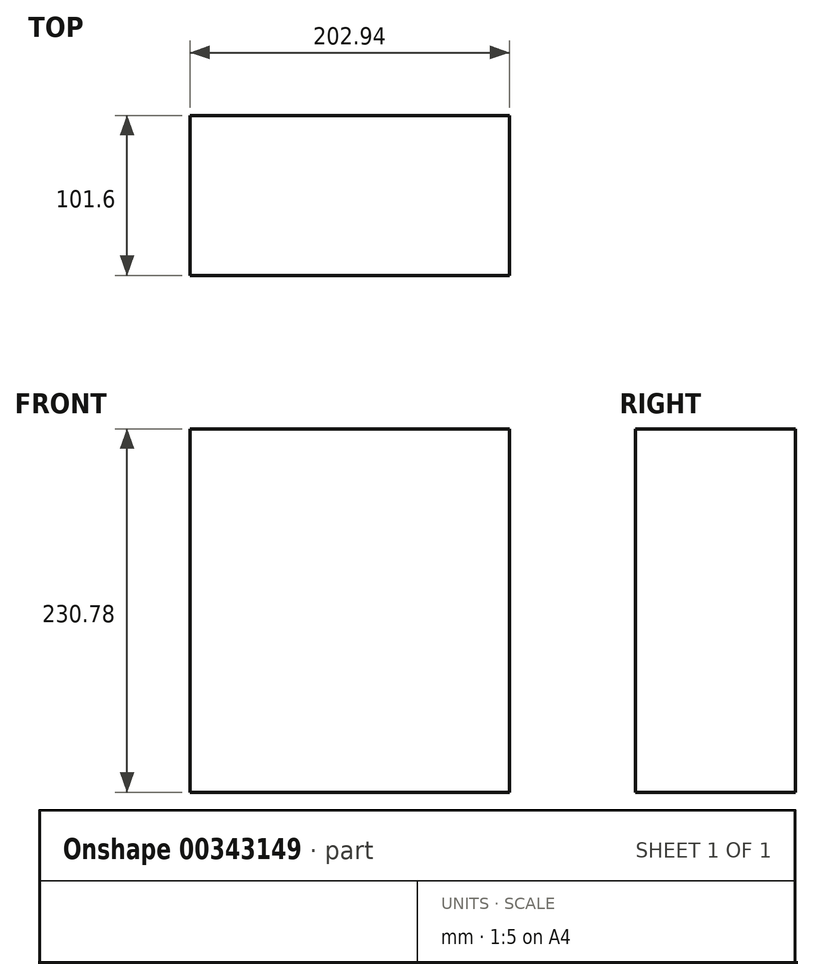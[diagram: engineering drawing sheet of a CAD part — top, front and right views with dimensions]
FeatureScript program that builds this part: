
annotation { "Feature Type Name" : "Feature", "Feature Type Description" : "" }
export const myFeature = defineFeature(function(context is Context, id is Id, definition is map)
    precondition{}
    {
        {
            var Q0;
            Q0=qCreatedBy(makeId("Front.planeOp"),FACE);
            var sketch = newSketch(context, id + "F0", { "sketchPlane" : qUnion([Q0])});
            skLineSegment(sketch, "E0.bottom", {"start": v(101.47, 115.4) * mm, "end": v(-101.47, 115.4) * mm});
            skLineSegment(sketch, "E0.top", {"start": v(101.47, -115.4) * mm, "end": v(-101.47, -115.4) * mm});
            skLineSegment(sketch, "E0.left", {"start": v(-101.47, -115.4) * mm, "end": v(-101.47, 115.4) * mm});
            skLineSegment(sketch, "E0.right", {"start": v(101.47, -115.4) * mm, "end": v(101.47, 115.4) * mm});
            skPoint(sketch, "E0.middle", {"position": v(0, 0) * mm});
            skSolve(sketch);
        }
        {
            var Q0;
            Q0=makeQuery(id+"F0.imprint","IMPRINT",FACE,{"disambiguationData":[TD([[makeQuery(id+"F0.imprint","IMPRINT",EDGE,{"derivedFrom":sQuery(id+"F0.wireOp",EDGE,"E0.bottom")}),1.0]])]});
            extrude(context, id + "F1", {"entities" : qUnion([Q0]), "depth" : 101.6 * mm});
        }
    });
